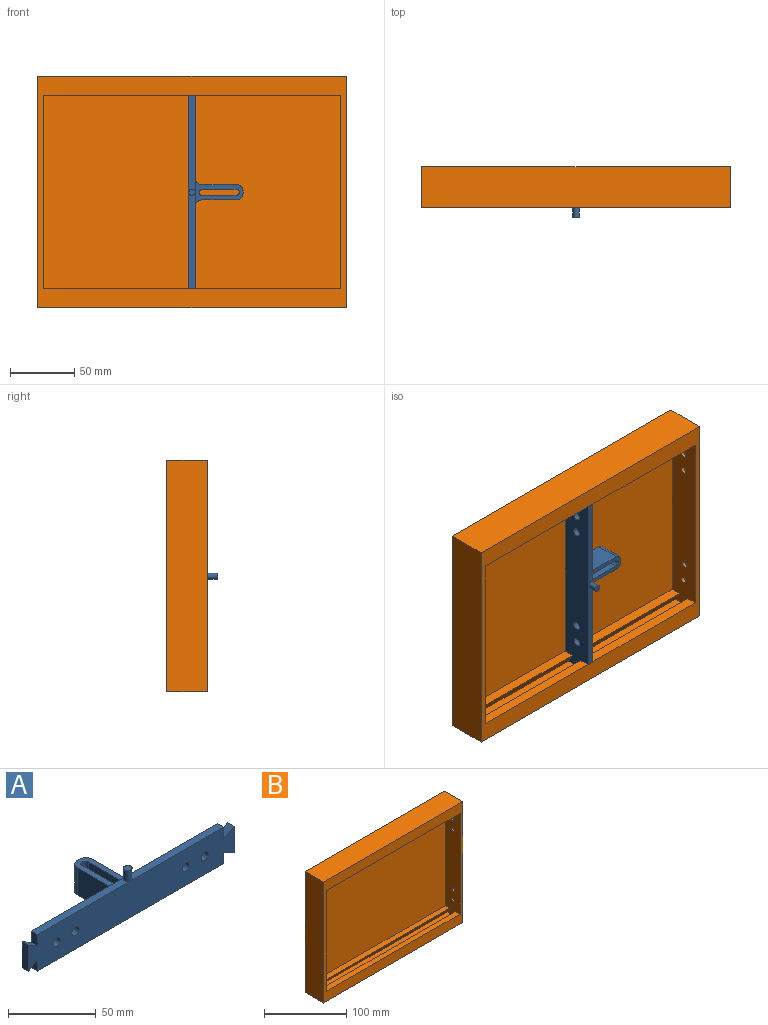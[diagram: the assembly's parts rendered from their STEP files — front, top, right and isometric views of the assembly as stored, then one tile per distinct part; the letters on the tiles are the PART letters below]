
ASSEMBLY  parts=2 mates=1
PART A: 33 faces, bbox 165.8x42.1x33 mm
  f0: plane 8x5mm, normal (1,0,0), area 40mm2, adj f15,f17,f18,f32
  f1: plane 8x5mm, normal (-1,0,0), area 40mm2, adj f2,f15,f17,f29
  f2: plane 75x5mm, normal (0,0,1), area 365.2mm2, adj f1,f15,f17,f19
  f3: plane 27.05x19.05mm, normal (-1,0,0), area 515.3mm2, adj f5,f10,f13,f25
  f4: plane 27.05x19.05mm, normal (1,0,0), area 515.3mm2, adj f5,f11,f13,f26
  f5: plane 37.13x22.16mm, normal (0,0,1), area 296mm2, adj f3,f4,f6,f7,f8,f9,f10,f11
  f6: plane 26.04x19.05mm, normal (1,0,0), area 496.1mm2, adj f5,f7,f12,f13
  f7: cylinder r=2.5mm len=19.05mm, axis (0,0,-1), area 149.6mm2, adj f5,f6,f8,f13
  f8: plane 26.04x19.05mm, normal (-1,0,0), area 496.1mm2, adj f5,f7,f12,f13
  f9: plane 19.05x2mm, normal (0,1,0), area 38.1mm2, adj f5,f10,f11,f13
  f10: cylinder r=5mm len=19.05mm, axis (0,0,-1), area 149.6mm2, adj f3,f5,f9,f13
  f11: cylinder r=5mm len=19.05mm, axis (0,0,-1), area 149.6mm2, adj f4,f5,f9,f13
  f12: cylinder r=2.5mm len=19.05mm, axis (0,0,-1), area 149.6mm2, adj f5,f6,f8,f13
  f13: plane 150x42.13mm, normal (0,0,-1), area 1046mm2, adj f3,f4,f6,f7,f8,f9,f10,f11
  f14: plane 8x5mm, normal (1,0,0), area 40mm2, adj f13,f15,f17,f30
  f15: plane 165.79x25.4mm, normal (0,1,0), area 3496.2mm2, adj f0,f1,f2,f5,f13,f14,f16,f18
  f16: plane 8x5mm, normal (-1,0,0), area 40mm2, adj f13,f15,f17,f28
  f17: plane 165.79x25.4mm, normal (0,-1,0), area 3918.4mm2, adj f0,f1,f2,f13,f14,f16,f18,f21
  f18: plane 75x5mm, normal (0,0,1), area 365.2mm2, adj f0,f15,f17,f19
  f19: cylinder r=2.5mm len=7.62mm, axis (0,0,-1), area 119.7mm2, adj f2,f18,f20
  f20: plane 5x5mm, normal (0,0,1), area 19.6mm2, adj f19
  f21: cylinder r=2.99mm len=5.97mm, axis (0,-1,0), area 93.8mm2, adj f15,f17
  f22: cylinder r=2.99mm len=5.97mm, axis (0,-1,0), area 93.8mm2, adj f15,f17
  f23: cylinder r=2.99mm len=5.97mm, axis (0,-1,0), area 93.8mm2, adj f15,f17
  f24: cylinder r=2.99mm len=5.97mm, axis (0,-1,0), area 93.8mm2, adj f15,f17
  f25: cylinder r=5.08mm len=19.05mm, axis (0,0,1), area 152mm2, adj f3,f5,f13,f15
  f26: cylinder r=5.08mm len=19.05mm, axis (0,0,-1), area 152mm2, adj f4,f5,f13,f15
  f27: plane 18.29x5mm, normal (-1,0,0), area 91.5mm2, adj f15,f17,f28,f29
  f28: plane 7.7x5mm, normal (0.5,0,-0.87), area 44.5mm2, adj f15,f16,f17,f27
  f29: plane 7.7x5mm, normal (0.5,0,0.87), area 44.5mm2, adj f1,f15,f17,f27
  f30: plane 8.09x5mm, normal (-0.5,0,-0.87), area 46.7mm2, adj f14,f15,f17,f31
  f31: plane 18.74x5mm, normal (1,0,0), area 93.7mm2, adj f15,f17,f30,f32
  f32: plane 8.09x5mm, normal (-0.5,0,0.87), area 46.7mm2, adj f0,f15,f17,f31
PART B: 35 faces, bbox 240x31.8x180 mm
  f0: plane 230x150mm, normal (0,-1,0), area 34500mm2, adj f1,f10,f17,f18
  f1: plane 230x7.94mm, normal (0,0,1), area 1825.6mm2, adj f0,f2,f17,f18
  f2: plane 230x7.5mm, normal (0,-0.87,-0.5), area 1991.9mm2, adj f1,f3,f17,f18
  f3: plane 230x18.19mm, normal (0,0,1), area 4182.6mm2, adj f2,f4,f17,f18
  f4: plane 230x7.5mm, normal (0,0.87,-0.5), area 1991.9mm2, adj f3,f5,f17,f18
  f5: plane 230x7.94mm, normal (0,0,1), area 1825.6mm2, adj f4,f16,f17,f18
  f6: plane 230x7.95mm, normal (0,0,-1), area 1828.5mm2, adj f7,f16,f17,f18
  f7: plane 230x7.5mm, normal (0,0.87,0.5), area 1991.9mm2, adj f6,f8,f17,f18
  f8: plane 230x18.19mm, normal (0,0,-1), area 4182.6mm2, adj f7,f9,f17,f18
  f9: plane 230x7.5mm, normal (0,-0.87,0.5), area 1991.9mm2, adj f8,f10,f17,f18
  f10: plane 230x7.93mm, normal (0,0,-1), area 1822.7mm2, adj f0,f9,f17,f18
  f11: plane 240x31.75mm, normal (0,0,-1), area 7620mm2, adj f12,f14,f15,f16
  f12: plane 180x31.75mm, normal (1,0,0), area 5715mm2, adj f11,f13,f15,f16
  f13: plane 240x31.75mm, normal (0,0,1), area 7620mm2, adj f12,f14,f15,f16
  f14: plane 180x31.75mm, normal (-1,0,0), area 5715mm2, adj f11,f13,f15,f16
  f15: plane 240x180mm, normal (0,1,0), area 43200mm2, adj f11,f12,f13,f14
  f16: plane 240x180mm, normal (0,-1,0), area 8700mm2, adj f5,f6,f11,f12,f13,f14,f17,f18
  f17: plane 165x25.4mm, normal (-1,0,0), area 3939.3mm2, adj f0,f1,f2,f3,f4,f5,f6,f7
  f18: plane 165x25.4mm, normal (1,0,0), area 3939.3mm2, adj f0,f1,f2,f3,f4,f5,f6,f7
  f19: cylinder r=2.5mm len=5mm, axis (-1,0,0), area 47.1mm2, adj f17,f20
  f20: plane 5x5mm, normal (-1,0,0), area 19.6mm2, adj f19
  f21: cylinder r=2.5mm len=5mm, axis (-1,0,0), area 47.1mm2, adj f17,f22
  f22: plane 5x5mm, normal (-1,0,0), area 19.6mm2, adj f21
  f23: cylinder r=2.5mm len=5mm, axis (-1,0,0), area 47.1mm2, adj f17,f24
  f24: plane 5x5mm, normal (-1,0,0), area 19.6mm2, adj f23
  f25: cylinder r=2.5mm len=5mm, axis (-1,0,0), area 47.1mm2, adj f17,f26
  f26: plane 5x5mm, normal (-1,0,0), area 19.6mm2, adj f25
  f27: cylinder r=2.5mm len=5mm, axis (1,0,0), area 47.1mm2, adj f18,f28
  f28: plane 5x5mm, normal (1,0,0), area 19.6mm2, adj f27
  f29: cylinder r=2.5mm len=5mm, axis (1,0,0), area 47.1mm2, adj f18,f30
  f30: plane 5x5mm, normal (1,0,0), area 19.6mm2, adj f29
  f31: cylinder r=2.5mm len=5mm, axis (1,0,0), area 47.1mm2, adj f18,f32
  f32: plane 5x5mm, normal (1,0,0), area 19.6mm2, adj f31
  f33: cylinder r=2.5mm len=5mm, axis (1,0,0), area 47.1mm2, adj f18,f34
  f34: plane 5x5mm, normal (1,0,0), area 19.6mm2, adj f33
PLACE A rot(axis=(0.58,0.58,-0.58),120deg) t=(37.27,-13.84,-173.7)mm
PLACE B t=(37.27,-7.5,-173.49)mm fixed
MATE planar A.f27 <-> B.f8  axis (0,0,1) through (37.27,-26.54,-90.99)mm
